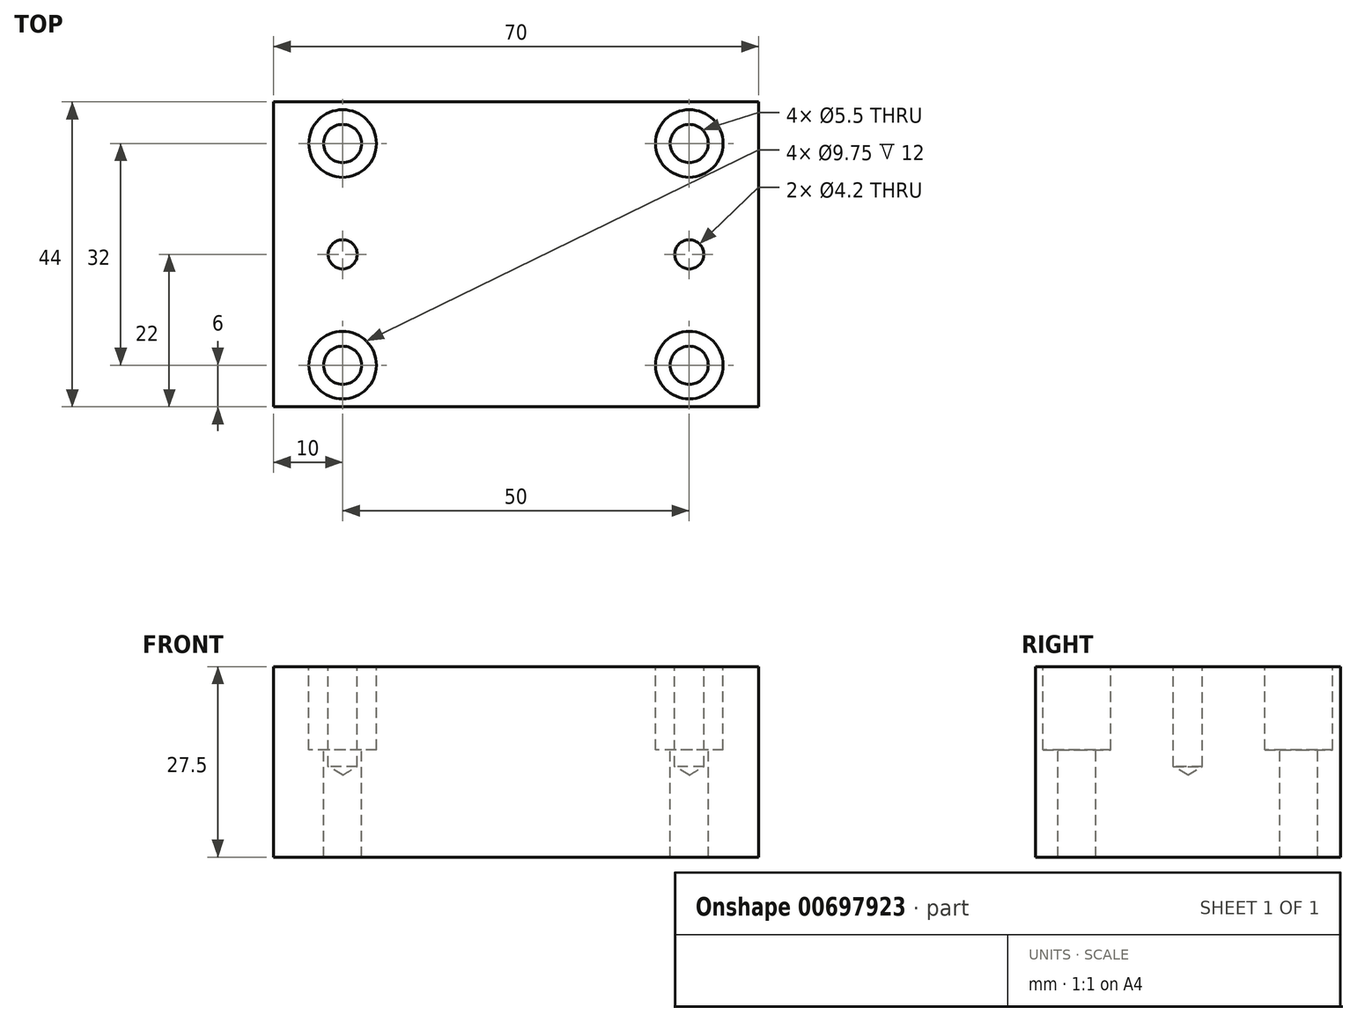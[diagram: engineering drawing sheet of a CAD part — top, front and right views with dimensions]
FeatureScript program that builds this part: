
annotation { "Feature Type Name" : "Feature", "Feature Type Description" : "" }
export const myFeature = defineFeature(function(context is Context, id is Id, definition is map)
    precondition{}
    {
        {
            var Q0;
            Q0=qCreatedBy(makeId("Top.planeOp"),FACE);
            var sketch = newSketch(context, id + "F0", { "sketchPlane" : qUnion([Q0])});
            skLineSegment(sketch, "E0.bottom", {"start": v(-35, -22) * mm, "end": v(35, -22) * mm});
            skLineSegment(sketch, "E0.top", {"start": v(-35, 22) * mm, "end": v(35, 22) * mm});
            skLineSegment(sketch, "E0.left", {"start": v(-35, -22) * mm, "end": v(-35, 22) * mm});
            skLineSegment(sketch, "E0.right", {"start": v(35, -22) * mm, "end": v(35, 22) * mm});
            skPoint(sketch, "E0.middle", {"position": v(0, 0) * mm});
            skSolve(sketch);
        }
        {
            var Q0;
            Q0 = qSketchRegion(id + "F0", true);
            extrude(context, id + "F1", {"entities" : qUnion([Q0]), "depth" : 27.5 * mm, "offsetDistance" : 25 * mm});
        }
        {
            var Q0;
            Q0=makeQuery(id+"F1.opExtrude","CAP_FACE",FACE,{"disambiguationData":[OSD([sQuery(id+"F0.wireOp",EDGE,"E0.bottom"),sQuery(id+"F0.wireOp",EDGE,"E0.top"),sQuery(id+"F0.wireOp",EDGE,"E0.left"),sQuery(id+"F0.wireOp",EDGE,"E0.right")])],"isStart":false});
            var sketch = newSketch(context, id + "F2", { "sketchPlane" : qUnion([Q0])});
            skCircle(sketch, "E1", {"center": v(25, 16) * mm, "radius": 4.5 * mm});
            skCircle(sketch, "E2", {"center": v(25, -16) * mm, "radius": 4.5 * mm});
            skCircle(sketch, "E3", {"center": v(-25, -16) * mm, "radius": 4.5 * mm});
            skCircle(sketch, "E4", {"center": v(-25, 16) * mm, "radius": 4.5 * mm});
            skSolve(sketch);
        }
        {
            var Q0;
            Q0=makeQuery(id+"F1.opExtrude","CAP_FACE",FACE,{"disambiguationData":[OSD([sQuery(id+"F0.wireOp",EDGE,"E0.bottom"),sQuery(id+"F0.wireOp",EDGE,"E0.top"),sQuery(id+"F0.wireOp",EDGE,"E0.left"),sQuery(id+"F0.wireOp",EDGE,"E0.right")])],"isStart":false});
            var sketch = newSketch(context, id + "F3", { "sketchPlane" : qUnion([Q0])});
            skPoint(sketch, "E5", {"position": v(25, 0) * mm});
            skPoint(sketch, "E6", {"position": v(-25, 0) * mm});
            skSolve(sketch);
        }
        {
            var Q0;
            Q0=sQuery(id+"F3.wireOp",VERTEX,"E5");
            var Q1;
            Q1=sQuery(id+"F3.wireOp",VERTEX,"E6");
            var Q2;
            Q2=makeQuery(id+"F1.opExtrude","SWEPT_BODY",BODY,{"disambiguationData":[OSD([sQuery(id+"F0.wireOp",EDGE,"E0.bottom"),sQuery(id+"F0.wireOp",EDGE,"E0.top"),sQuery(id+"F0.wireOp",EDGE,"E0.left"),sQuery(id+"F0.wireOp",EDGE,"E0.right")])]});
            hole(context, id + "F4", {"style" : HoleStyle.SIMPLE, "endStyle" : HoleEndStyle.BLIND, "standardTappedOrClearance" : lookupTablePath({ "standard" : "ISO", "engagement" : "75%", "pitch" : "0.8 mm", "size" : "M5", "type" : "Tapped" }), "standardBlindInLast" : lookupTablePath({ "standard" : "ISO", "engagement" : "75%", "pitch" : "0.8 mm", "size" : "M5", "type" : "Tapped" }), "holeDiameter" : 4.2 * mm, "majorDiameter" : 5 * mm, "showTappedDepth" : true, "holeDepth" : 14.4 * mm, "isTappedThrough" : true, "tappedDepth" : 12 * mm, "tapClearance" : 3, "locations" : qUnion([Q0, Q1]), "scope" : qUnion([Q2])});
        }
        {
            var Q0;
            Q0=sQuery(id+"F2.wireOp",VERTEX,"E2.center");
            var Q1;
            Q1=sQuery(id+"F2.wireOp",VERTEX,"E1.center");
            var Q2;
            Q2=sQuery(id+"F2.wireOp",VERTEX,"E3.center");
            var Q3;
            Q3=sQuery(id+"F2.wireOp",VERTEX,"E4.center");
            var Q4;
            Q4=makeQuery(id+"F1.opExtrude","SWEPT_BODY",BODY,{"disambiguationData":[OSD([sQuery(id+"F0.wireOp",EDGE,"E0.bottom"),sQuery(id+"F0.wireOp",EDGE,"E0.top"),sQuery(id+"F0.wireOp",EDGE,"E0.left"),sQuery(id+"F0.wireOp",EDGE,"E0.right")])]});
            hole(context, id + "F5", {"style" : HoleStyle.C_BORE, "endStyle" : HoleEndStyle.THROUGH, "holeDiameter" : 5.5 * mm, "cBoreDiameter" : 9.75 * mm, "cBoreDepth" : 12 * mm, "majorDiameter" : 5 * mm, "isTappedThrough" : true, "tappedDepth" : 10.4 * mm, "tapClearance" : 3, "locations" : qUnion([Q0, Q1, Q2, Q3]), "scope" : qUnion([Q4])});
        }
    });
